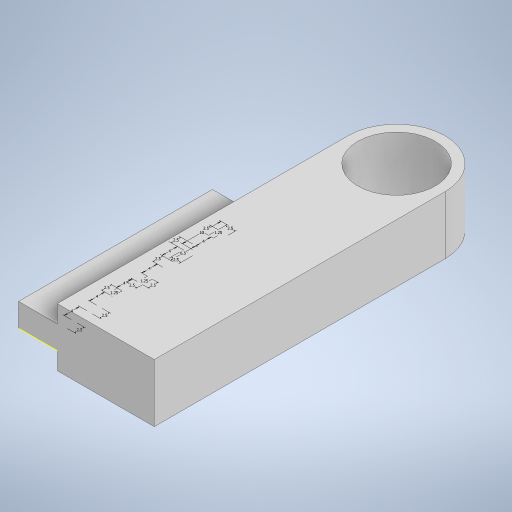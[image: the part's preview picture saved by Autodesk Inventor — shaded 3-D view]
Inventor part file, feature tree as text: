
AUTODESK INVENTOR PART (.ipt)
format: ipt  version: 2023 (Build 270158000, 158)  size: 274,944 bytes
history: native  units: mm
features: sketch x7, extrude x3
ambient origin geometry x8: Origin, YZ Plane, XZ Plane, XY Plane, X Axis, Y Axis, Z Axis, Center Point
bodies: Solid1 (feature_tree)
feature tree (10):
  extrude  "Extrusion1"  Depth=25.0mm
  extrude  "Extrusion2"  Depth=15.0mm TaperAngle=0.0deg
  sketch  "Sketch3"  dims[d5=50.0mm d8=3.0mm]
  extrude  "Extrusion3"  Depth=50.0mm
  sketch  "Sketch5"  dims[d10=50.0mm]
  sketch  "Sketch6"  dims[d11=10.0mm d12=0.0mm]
  sketch  "Sketch7"  dims[d13=25.0mm d14=0.0mm d15=10.0mm d16=2.5mm d17=2.5mm d18=4.0mm d19=2.5mm d20=4.0mm d21=1.25mm d22=2.5mm d23=2.5mm d24=4.0mm d25=1.25mm d26=2.5mm d27=4.0mm d28=2.5mm d29=4.0mm d30=2.5mm d31=6.5mm d32=4.0mm d33=1.25mm d34=2.5mm d35=2.5mm]
  sketch  "Sketch1"  dims[d0=20.0mm d1=25.0mm]
  sketch  "Sketch2"  dims[d2=50.0mm d3=15.0mm d4=0.0mm]
  sketch  "Sketch4"  dims[d9=6.0mm]
